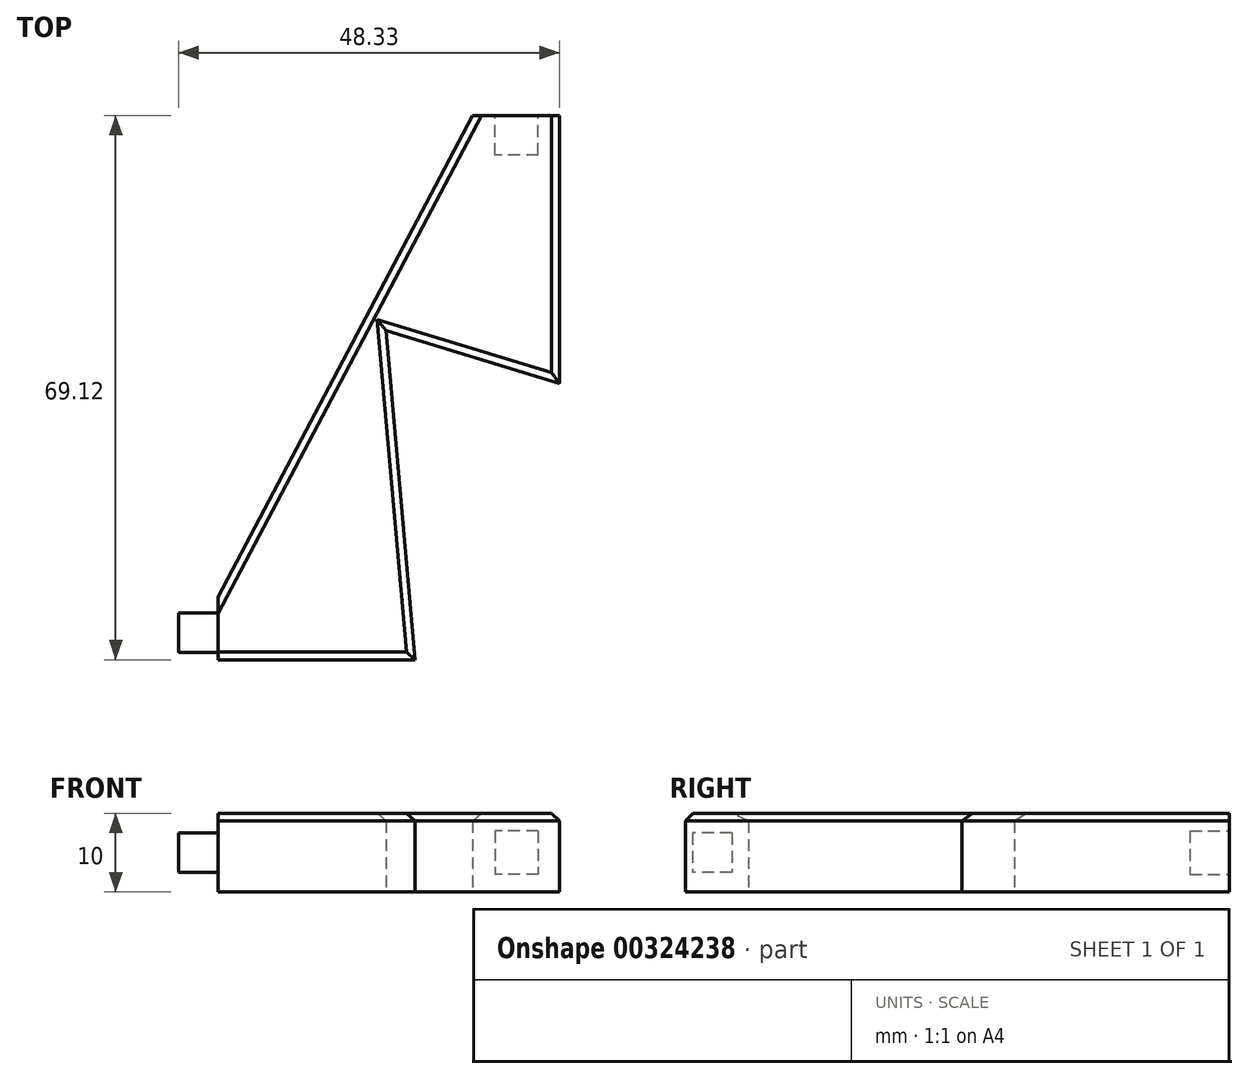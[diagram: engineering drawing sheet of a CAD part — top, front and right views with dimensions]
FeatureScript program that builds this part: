
annotation { "Feature Type Name" : "Feature", "Feature Type Description" : "" }
export const myFeature = defineFeature(function(context is Context, id is Id, definition is map)
    precondition{}
    {
        {
            var Q0;
            Q0=qCreatedBy(makeId("Top.planeOp"),FACE);
            var sketch = newSketch(context, id + "F0", { "sketchPlane" : qUnion([Q0])});
            skLineSegment(sketch, "E0", {"start": v(0, 0) * mm, "end": v(0, -8) * mm});
            skLineSegment(sketch, "E1", {"start": v(0, -8) * mm, "end": v(25, -8) * mm});
            skLineSegment(sketch, "E2", {"start": v(25, -8) * mm, "end": v(21.34, 33.84) * mm});
            skLineSegment(sketch, "E3", {"start": v(21.34, 33.84) * mm, "end": v(43.33, 27.12) * mm});
            skLineSegment(sketch, "E4", {"start": v(43.33, 27.12) * mm, "end": v(43.33, 61.12) * mm});
            skLineSegment(sketch, "E5", {"start": v(43.33, 61.12) * mm, "end": v(32.33, 61.12) * mm});
            skLineSegment(sketch, "E6", {"start": v(0, 0) * mm, "end": v(32.33, 61.12) * mm});
            skSolve(sketch);
        }
        {
            var Q0;
            Q0 = qSketchRegion(id + "F0", true);
            extrude(context, id + "F1", {"entities" : qUnion([Q0]), "depth" : 10 * mm});
        }
        {
            var Q0;
            Q0=makeQuery(id+"F1.opExtrude","CAP_EDGE",EDGE,{"disambiguationData":[OSD([sQuery(id+"F0.wireOp",EDGE,"E6")])],"isStart":false});
            var Q1;
            Q1=makeQuery(id+"F1.opExtrude","CAP_EDGE",EDGE,{"disambiguationData":[OSD([sQuery(id+"F0.wireOp",EDGE,"E1")])],"isStart":false});
            var Q2;
            Q2=makeQuery(id+"F1.opExtrude","CAP_EDGE",EDGE,{"disambiguationData":[OSD([sQuery(id+"F0.wireOp",EDGE,"E2")])],"isStart":false});
            var Q3;
            Q3=makeQuery(id+"F1.opExtrude","CAP_EDGE",EDGE,{"disambiguationData":[OSD([sQuery(id+"F0.wireOp",EDGE,"E3")])],"isStart":false});
            var Q4;
            Q4=makeQuery(id+"F1.opExtrude","CAP_EDGE",EDGE,{"disambiguationData":[OSD([sQuery(id+"F0.wireOp",EDGE,"E4")])],"isStart":false});
            chamfer(context, id + "F2", {"entities" : qUnion([Q0, Q1, Q2, Q3, Q4]), "width" : 1 * mm, "tangentPropagation" : true});
        }
        {
            var Q0;
            Q0=makeQuery(id+"F1.opExtrude","SWEPT_FACE",FACE,{"disambiguationData":[OSD([sQuery(id+"F0.wireOp",EDGE,"E0")])]});
            var sketch = newSketch(context, id + "F3", { "sketchPlane" : qUnion([Q0])});
            skLineSegment(sketch, "E7", {"start": v(4.57, 10) * mm, "end": v(4.57, 0) * mm});
            skLineSegment(sketch, "E8.bottom", {"start": v(2.07, 7.5) * mm, "end": v(7.07, 7.5) * mm});
            skLineSegment(sketch, "E8.top", {"start": v(2.07, 2.5) * mm, "end": v(7.07, 2.5) * mm});
            skLineSegment(sketch, "E8.left", {"start": v(2.07, 7.5) * mm, "end": v(2.07, 2.5) * mm});
            skLineSegment(sketch, "E8.right", {"start": v(7.07, 7.5) * mm, "end": v(7.07, 2.5) * mm});
            skPoint(sketch, "E8.middle", {"position": v(4.57, 5) * mm});
            skSolve(sketch);
        }
        {
            var Q0;
            Q0 = qSketchRegion(id + "F3", true);
            extrude(context, id + "F4", {"entities" : qUnion([Q0]), "operationType" : NewBodyOperationType.ADD, "depth" : 5 * mm});
        }
        {
            var Q0;
            Q0=makeQuery(id+"F1.opExtrude","SWEPT_FACE",FACE,{"disambiguationData":[OSD([sQuery(id+"F0.wireOp",EDGE,"E5")])]});
            var sketch = newSketch(context, id + "F5", { "sketchPlane" : qUnion([Q0])});
            skLineSegment(sketch, "E9", {"start": v(-37.9, 10) * mm, "end": v(-37.9, 0) * mm});
            skLineSegment(sketch, "E10.bottom", {"start": v(-40.65, 7.75) * mm, "end": v(-35.15, 7.75) * mm});
            skLineSegment(sketch, "E10.top", {"start": v(-40.65, 2.25) * mm, "end": v(-35.15, 2.25) * mm});
            skLineSegment(sketch, "E10.left", {"start": v(-40.65, 7.75) * mm, "end": v(-40.65, 2.25) * mm});
            skLineSegment(sketch, "E10.right", {"start": v(-35.15, 7.75) * mm, "end": v(-35.15, 2.25) * mm});
            skPoint(sketch, "E10.middle", {"position": v(-37.9, 5) * mm});
            skSolve(sketch);
        }
        {
            var Q0;
            {var subQ5=sQuery(id+"F5.wireOp",EDGE,"E10.right");Q0=makeQuery(id+"F5.imprint","IMPRINT",FACE,{"disambiguationData":[TD([[makeQuery(id+"F5.imprint","IMPRINT",EDGE,{"derivedFrom":subQ5}),-1.0]])]});}
            var Q1;
            {var subQ5=sQuery(id+"F5.wireOp",EDGE,"E10.left");Q1=makeQuery(id+"F5.imprint","IMPRINT",FACE,{"disambiguationData":[TD([[makeQuery(id+"F5.imprint","IMPRINT",EDGE,{"derivedFrom":subQ5}),1.0]])]});}
            extrude(context, id + "F6", {"entities" : qUnion([Q0, Q1]), "operationType" : NewBodyOperationType.REMOVE, "oppositeDirection" : true, "depth" : 5 * mm});
        }
    });
